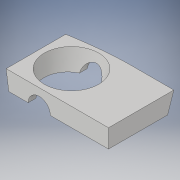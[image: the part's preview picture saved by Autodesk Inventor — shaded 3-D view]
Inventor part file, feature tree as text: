
AUTODESK INVENTOR PART (.ipt)
format: ipt  version: 2018 (Build 220112000, 112)  size: 159,232 bytes
history: native  units: in
note: dims shown in document units (in); Inventor stores cm internally (conversion verified against a paired STEP export)
features: sketch x6, loft x2, extrude x2, plane x1
ambient origin geometry x8: Origin, YZ Plane, XZ Plane, XY Plane, X Axis, Y Axis, Z Axis, Center Point
bodies: Solid1 (feature_tree)
feature tree (11):
  sketch  "Sketch1"  dims[d1=0.8in d2=1.35in]
  plane  "Work Plane1"
  loft  "Loft1"
  loft  "Loft2"
  extrude  "Extrusion1"  Depth=0.875in
  extrude  "Extrusion2"  TaperAngle=0.0deg  [1 undecoded]
  sketch  "Sketch3"  dims[d4=0.4in d5=2.8in]
  sketch  "Sketch4"  dims[d15=0.875in d17=0.875in]
  sketch  "Sketch5"  dims[d18=0.875in d19=0.0in d20=90.0deg]
  sketch  "Sketch6"  dims[d21=0.0in d22=90.0deg]
  sketch  "Sketch7"  dims[d23=1.6in d24=0.875in d26=0.875in d27=0.65in d28=0.0in d29=90.0deg d30=0.0in d31=90.0deg d32=0.4in d33=0.4in d34=0.4in d35=0.15in d36=0.0in d37=0.0in d38=3.0in d39=0.0in d40=2.55in d41=0.0in]
note: 1 required parameter value undecoded (feature->parameter linkage not recoverable at this tier; creation-order binding heuristic only, values carry confidence <= 0.55)
